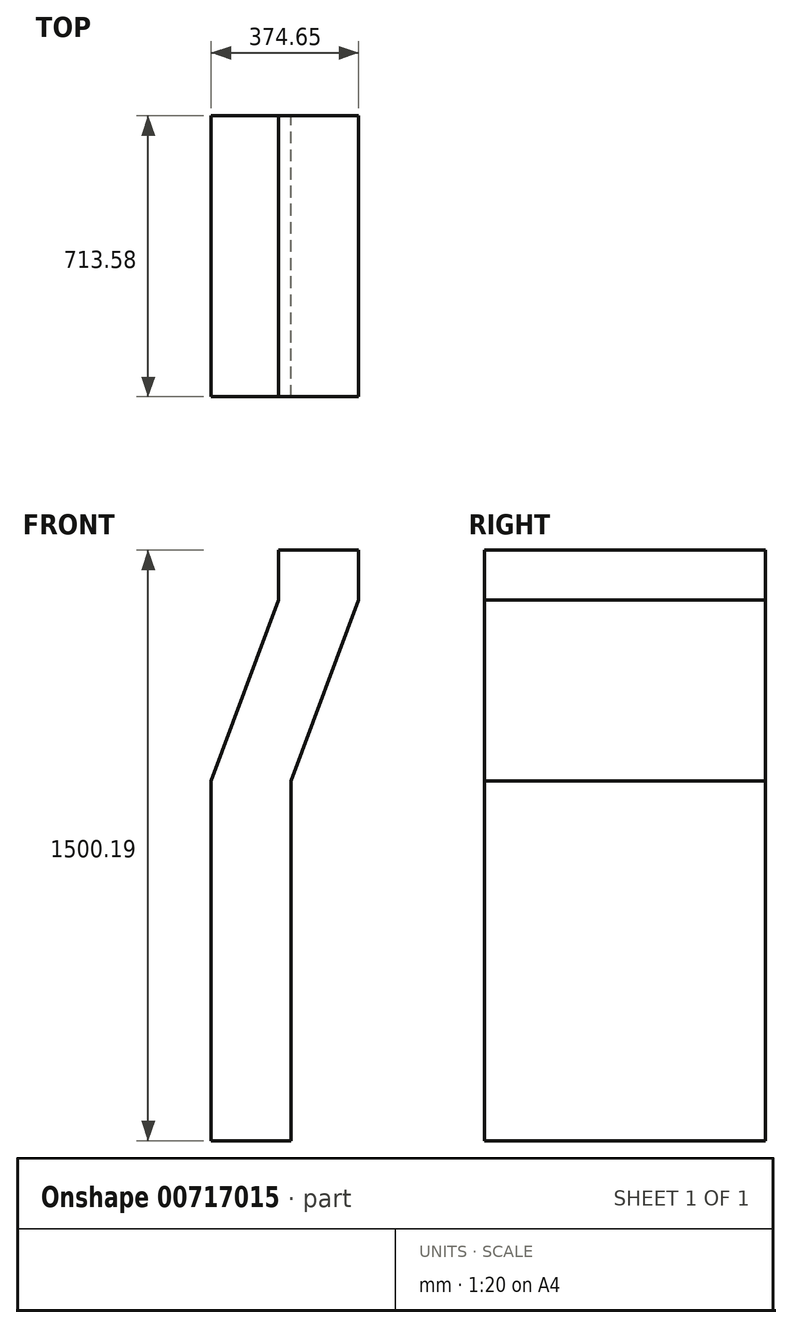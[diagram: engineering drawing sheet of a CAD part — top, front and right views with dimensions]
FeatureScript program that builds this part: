
annotation { "Feature Type Name" : "Feature", "Feature Type Description" : "" }
export const myFeature = defineFeature(function(context is Context, id is Id, definition is map)
    precondition{}
    {
        {
            var Q0;
            Q0=qCreatedBy(makeId("Front.planeOp"),FACE);
            var sketch = newSketch(context, id + "F0", { "sketchPlane" : qUnion([Q0])});
            skLineSegment(sketch, "E0.bottom", {"start": v(0, 0) * mm, "end": v(203.2, 0) * mm});
            skLineSegment(sketch, "E0.left", {"start": v(0, 0) * mm, "end": v(0, 914.4) * mm});
            skLineSegment(sketch, "E0.right", {"start": v(203.2, 0) * mm, "end": v(203.2, 914.4) * mm});
            skLineSegment(sketch, "E1", {"start": v(0, 914.4) * mm, "end": v(171.45, 1373.19) * mm});
            skLineSegment(sketch, "E2", {"start": v(171.45, 1500.19) * mm, "end": v(171.45, 1373.19) * mm});
            skLineSegment(sketch, "E3", {"start": v(171.45, 1500.19) * mm, "end": v(374.65, 1500.19) * mm});
            skLineSegment(sketch, "E4", {"start": v(374.65, 1500.19) * mm, "end": v(374.65, 1373.19) * mm});
            skLineSegment(sketch, "E5", {"start": v(374.65, 1373.19) * mm, "end": v(203.2, 914.4) * mm});
            skLineSegment(sketch, "E6", {"start": v(171.45, 1373.19) * mm, "end": v(374.65, 1373.19) * mm, "construction": true});
            skLineSegment(sketch, "E7", {"start": v(0, 914.4) * mm, "end": v(203.2, 914.4) * mm, "construction": true});
            skSolve(sketch);
        }
        {
            var Q0;
            Q0 = qSketchRegion(id + "F0", true);
            extrude(context, id + "F1", {"entities" : qUnion([Q0]), "depth" : 713.58 * mm, "offsetDistance" : 25.4 * mm});
        }
    });
